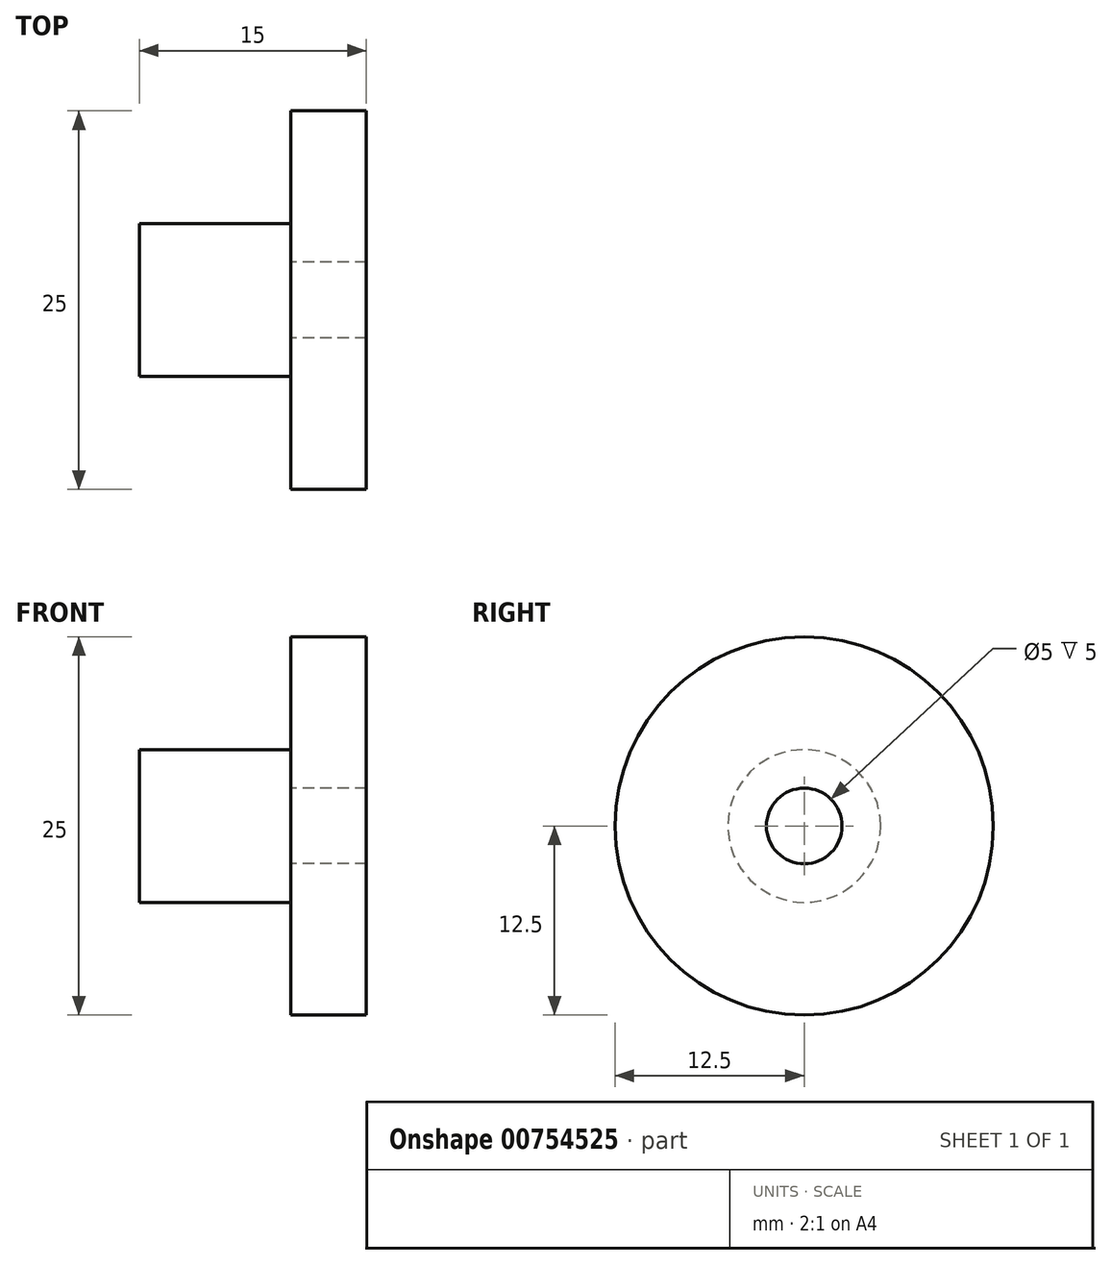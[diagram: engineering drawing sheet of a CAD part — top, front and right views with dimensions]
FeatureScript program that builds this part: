
annotation { "Feature Type Name" : "Feature", "Feature Type Description" : "" }
export const myFeature = defineFeature(function(context is Context, id is Id, definition is map)
    precondition{}
    {
        {
            var Q0;
            Q0=qCreatedBy(makeId("Right.planeOp"),FACE);
            var sketch = newSketch(context, id + "F0", { "sketchPlane" : qUnion([Q0])});
            skCircle(sketch, "E0", {"center": v(0, 0) * mm, "radius": 12.5 * mm});
            skSolve(sketch);
        }
        {
            var Q0;
            Q0=qCreatedBy(makeId("Right.planeOp"),FACE);
            var sketch = newSketch(context, id + "F1", { "sketchPlane" : qUnion([Q0])});
            skCircle(sketch, "E1", {"center": v(0, 0) * mm, "radius": 2.5 * mm});
            skSolve(sketch);
        }
        {
            var Q0;
            Q0=qCreatedBy(makeId("Right.planeOp"),FACE);
            var sketch = newSketch(context, id + "F2", { "sketchPlane" : qUnion([Q0])});
            skCircle(sketch, "E2", {"center": v(0, 0) * mm, "radius": 2.5 * mm});
            skSolve(sketch);
        }
        {
            var Q0;
            Q0 = qSketchRegion(id + "F0", true);
            extrude(context, id + "F3", {"entities" : qUnion([Q0]), "depth" : 5 * mm, "offsetDistance" : 25 * mm});
        }
        {
            var Q0;
            Q0 = qSketchRegion(id + "F1", true);
            extrude(context, id + "F4", {"entities" : qUnion([Q0]), "operationType" : NewBodyOperationType.REMOVE, "depth" : 10 * mm, "offsetDistance" : 25 * mm});
        }
        {
            var Q0;
            Q0=makeQuery(id+"F2.imprint","IMPRINT",FACE,{"disambiguationData":[TD([[makeQuery(id+"F2.imprint","IMPRINT",EDGE,{"derivedFrom":sQuery(id+"F2.wireOp",EDGE,"E2")}),1.0]])]});
            var sketch = newSketch(context, id + "F5", { "sketchPlane" : qUnion([Q0])});
            skCircle(sketch, "E3", {"center": v(0, 0) * mm, "radius": 5 * mm});
            skSolve(sketch);
        }
        {
            var Q0;
            Q0=makeQuery(id+"F2.imprint","IMPRINT",FACE,{"disambiguationData":[TD([[makeQuery(id+"F2.imprint","IMPRINT",EDGE,{"derivedFrom":sQuery(id+"F2.wireOp",EDGE,"E2")}),1.0]])]});
            extrude(context, id + "F6", {"entities" : qUnion([Q0]), "operationType" : NewBodyOperationType.REMOVE, "depth" : 3 * mm, "offsetDistance" : 25 * mm});
        }
        {
            var Q0;
            Q0=makeQuery(id+"F5.imprint","IMPRINT",FACE,{"disambiguationData":[TD([[makeQuery(id+"F5.imprint","IMPRINT",EDGE,{"derivedFrom":sQuery(id+"F5.wireOp",EDGE,"E3")}),1.0]])]});
            var sketch = newSketch(context, id + "F7", { "sketchPlane" : qUnion([Q0])});
            skCircle(sketch, "E4", {"center": v(0, 0) * mm, "radius": 5.05 * mm});
            skSolve(sketch);
        }
        {
            var Q0;
            Q0 = qSketchRegion(id + "F7", true);
            extrude(context, id + "F8", {"entities" : qUnion([Q0]), "operationType" : NewBodyOperationType.ADD, "oppositeDirection" : true, "depth" : 10 * mm, "offsetDistance" : 25 * mm});
        }
    });
